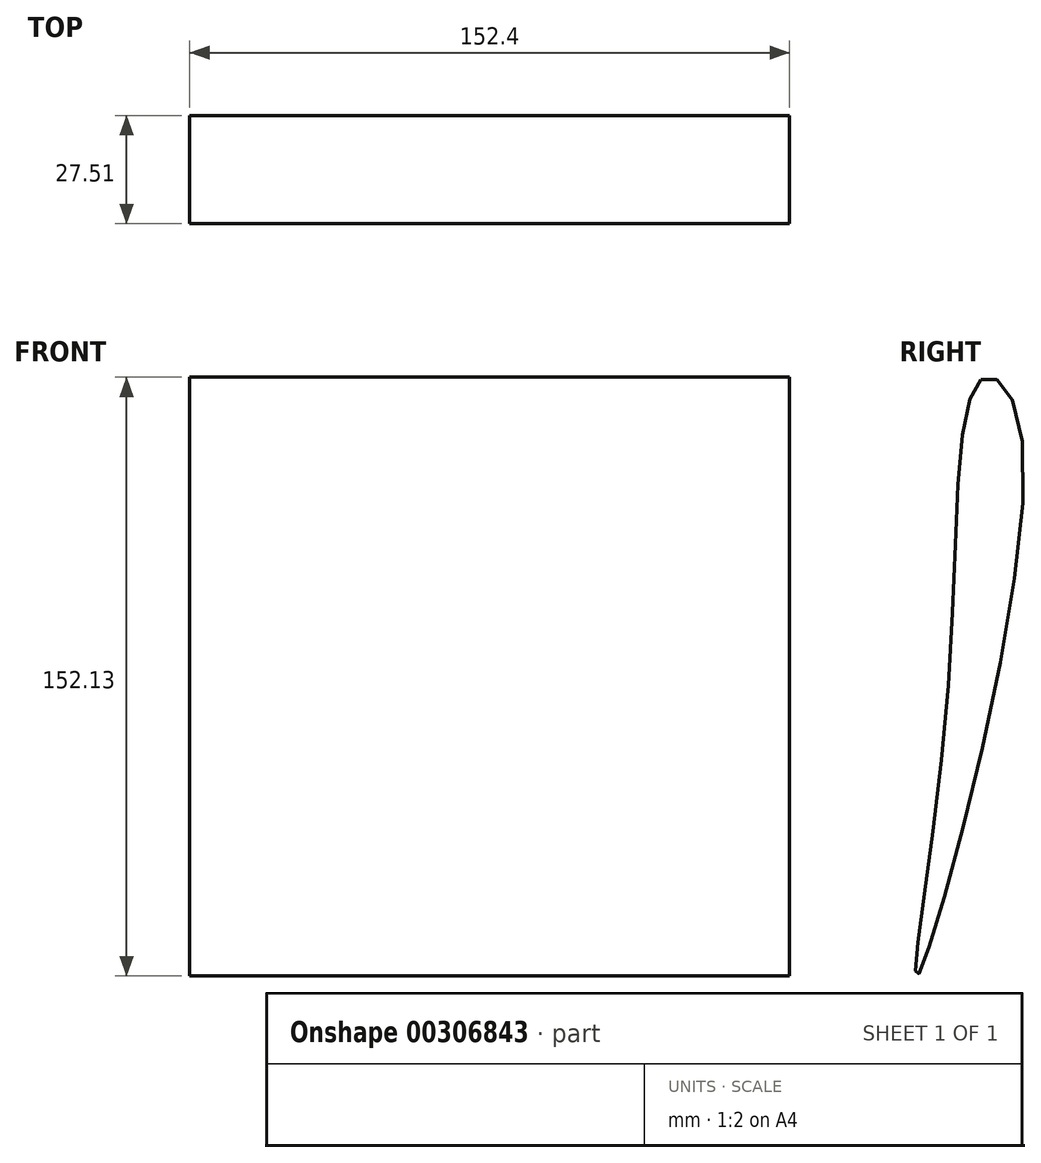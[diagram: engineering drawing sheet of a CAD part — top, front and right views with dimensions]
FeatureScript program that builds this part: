
annotation { "Feature Type Name" : "Feature", "Feature Type Description" : "" }
export const myFeature = defineFeature(function(context is Context, id is Id, definition is map)
    precondition{}
    {
        {
            var Q0;
            Q0=qCreatedBy(makeId("Right.planeOp"),FACE);
            var sketch = newSketch(context, id + "F0", { "sketchPlane" : qUnion([Q0])});
            skFitSpline(sketch, "E0", {"points": [v(13.84, 74.5) * mm, v(24.2, 60.3) * mm, v(-2.03, -76.46) * mm, v(5.04, -9.14) * mm, v(13.84, 74.5) * mm]});
            skSolve(sketch);
        }
        {
            var Q0;
            Q0=makeQuery(id+"F0.imprint","IMPRINT",FACE,{"disambiguationData":[TD([[makeQuery(id+"F0.imprint","IMPRINT",EDGE,{"derivedFrom":sQuery(id+"F0.wireOp",EDGE,"E0")}),-1.0]])]});
            extrude(context, id + "F1", {"entities" : qUnion([Q0]), "depth" : 76.2 * mm, "hasSecondDirection" : true, "secondDirectionOppositeDirection" : true, "secondDirectionDepth" : 76.2 * mm});
        }
    });
